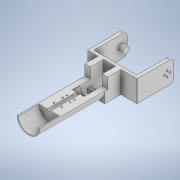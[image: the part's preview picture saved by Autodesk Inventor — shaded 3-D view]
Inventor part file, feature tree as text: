
AUTODESK INVENTOR PART (.ipt)
format: ipt  version: 2022 (Build 260153000, 153)  size: 386,048 bytes
history: native  units: mm
features: sketch x21, extrude x20, fillet x2, plane x1
ambient origin geometry x8: Origin, YZ Plane, XZ Plane, XY Plane, X Axis, Y Axis, Z Axis, Center Point
bodies: Solid1 (feature_tree)
feature tree (44):
  extrude  "Extrusion1"  Depth=80.0mm
  extrude  "Extrusion2"  Depth=40.0mm TaperAngle=0.0deg
  extrude  "Extrusion3"  Depth=3.0mm
  fillet  "Fillet1"  Radius=40.0mm
  extrude  "Extrusion4"  Depth=4.0mm
  extrude  "Extrusion5"  Depth=10.0mm TaperAngle=0.0deg
  extrude  "Extrusion6"  Depth=11.0mm
  extrude  "Extrusion7"  Depth=5.0mm
  extrude  "Extrusion8"  Depth=24.0mm TaperAngle=0.0deg
  extrude  "Extrusion9"  Depth=6.0mm TaperAngle=0.0deg
  extrude  "Extrusion10"  Depth=33.7mm
  extrude  "Extrusion11"  Depth=13.8mm TaperAngle=0.0deg
  extrude  "Extrusion12"  Depth=50.0mm TaperAngle=0.0deg
  fillet  "Fillet3"  Radius=50.0mm
  extrude  "Extrusion19"  Depth=38.0mm
  extrude  "Extrusion20"  Depth=6.2mm TaperAngle=0.0deg
  extrude  "Extrusion21"  Depth=10.0mm TaperAngle=0.0deg
  extrude  "Extrusion22"  Depth=10.0mm TaperAngle=0.0deg
  extrude  "Extrusion23"  Depth=10.0mm TaperAngle=0.0deg
  extrude  "Extrusion24"  Depth=4.0mm
  extrude  "Extrusion25"  Depth=6.0mm
  sketch  "Sketch27"  dims[d92=10.0mm d93=0.0mm d95=4.4mm]
  plane  "Work Plane2"
  extrude  "Extrusion26"  Depth=10.0mm
  sketch  "Sketch1"  dims[d0=62.0mm d1=80.0mm]
  sketch  "Sketch2"  dims[d2=6.0mm d3=40.0mm d4=0.0mm]
  sketch  "Sketch3"  dims[d5=62.0mm d9=3.0mm d10=40.0mm d12=360.0deg]
  sketch  "Sketch4"  dims[d14=40.0mm d15=0.0mm d16=4.0mm]
  sketch  "Sketch5"  dims[d18=11.5mm d19=10.0mm d20=0.0mm]
  sketch  "Sketch6"  dims[d21=8.0mm d22=11.0mm]
  sketch  "Sketch8"  dims[d23=11.0mm d24=5.0mm]
  sketch  "Sketch9"  dims[d25=5.0mm d26=24.0mm d27=0.0mm]
  sketch  "Sketch10"  dims[d29=6.0mm d30=6.0mm d31=0.0mm]
  sketch  "Sketch11"  dims[d32=13.8mm d33=0.0mm d37=33.7mm]
  sketch  "Sketch12"  dims[d38=11.0mm d39=13.8mm d40=0.0mm]
  sketch  "Sketch13"  dims[d41=6.0mm d42=50.0mm d43=0.0mm d44=50.0mm d45=0.0mm]
  sketch  "Sketch20"  dims[d47=36.0mm d48=0.0mm d49=38.0mm]
  sketch  "Sketch21"  dims[d50=32.0mm d51=0.0mm d52=6.2mm d53=0.0mm]
  sketch  "Sketch22"  dims[d63=1.0mm d69=10.0mm d70=0.0mm]
  sketch  "Sketch23"  dims[d71=10.0mm d72=0.0mm d73=10.0mm d74=0.0mm]
  sketch  "Sketch24"  dims[d75=10.0mm d76=0.0mm d77=10.0mm d78=0.0mm]
  sketch  "Sketch25"  dims[d84=0.0mm d85=0.0mm d86=4.0mm]
  sketch  "Sketch26"  dims[d90=2.5mm d91=6.0mm]
  sketch  "Sketch28"  dims[d96=4.2mm d97=0.0mm]
